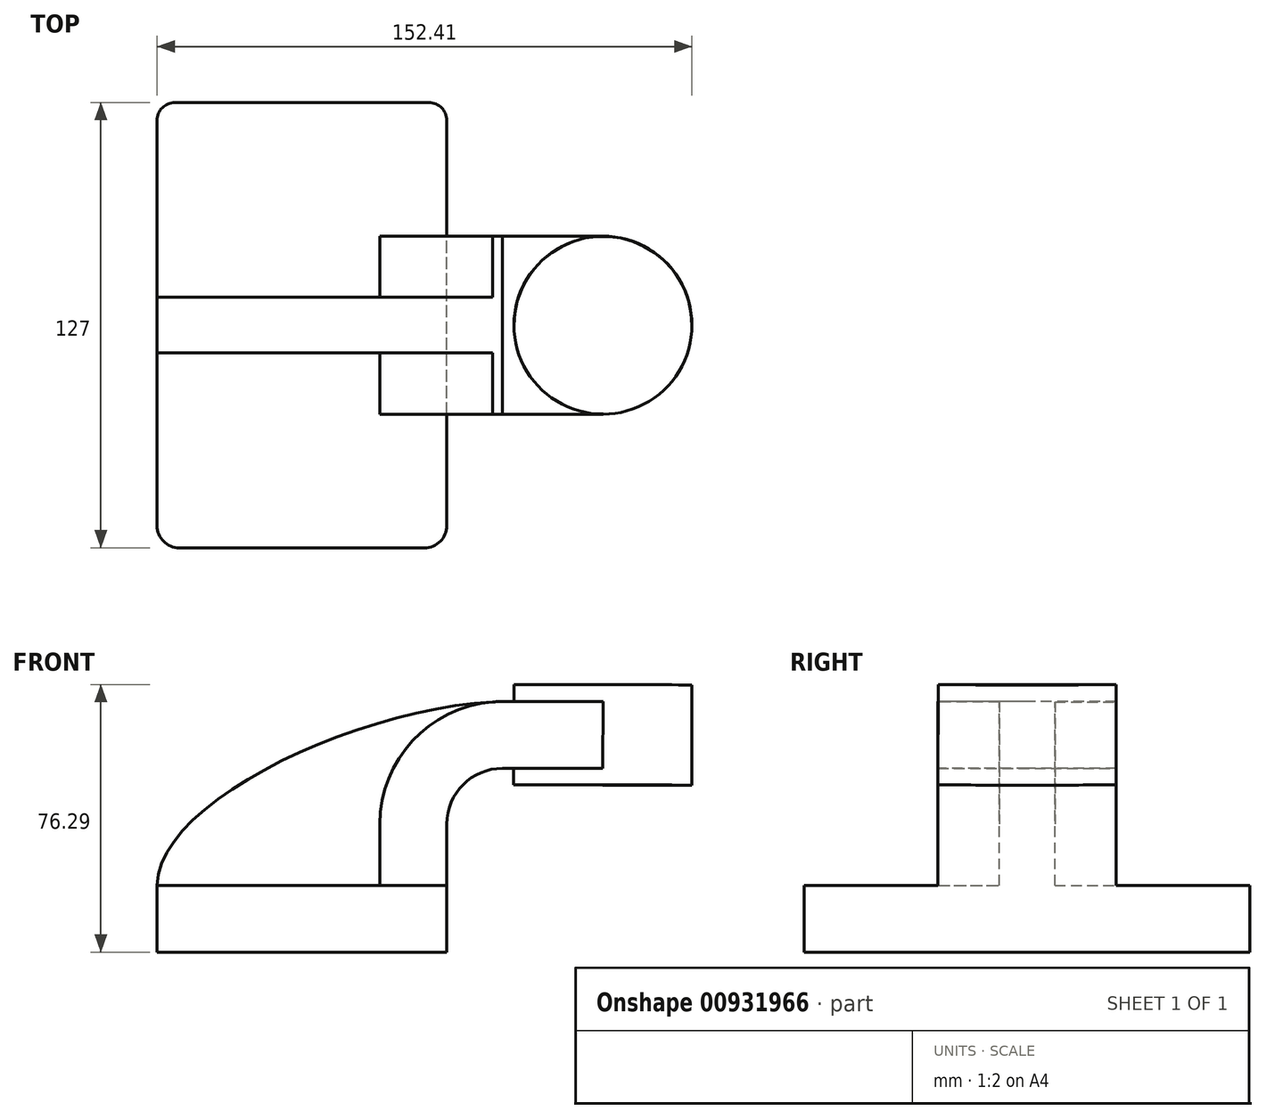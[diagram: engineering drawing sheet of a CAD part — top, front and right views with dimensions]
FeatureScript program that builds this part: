
annotation { "Feature Type Name" : "Feature", "Feature Type Description" : "" }
export const myFeature = defineFeature(function(context is Context, id is Id, definition is map)
    precondition{}
    {
        {
            var Q0;
            Q0=qCreatedBy(makeId("Front.planeOp"),FACE);
            var sketch = newSketch(context, id + "F0", { "sketchPlane" : qUnion([Q0])});
            skLineSegment(sketch, "E0.bottom", {"start": v(41.28, -9.52) * mm, "end": v(-41.28, -9.53) * mm});
            skLineSegment(sketch, "E0.top", {"start": v(41.27, 9.53) * mm, "end": v(-41.28, 9.53) * mm});
            skLineSegment(sketch, "E0.left", {"start": v(41.28, -9.52) * mm, "end": v(41.28, 9.53) * mm});
            skLineSegment(sketch, "E0.right", {"start": v(-41.28, -9.53) * mm, "end": v(-41.28, 9.53) * mm});
            skPoint(sketch, "E0.middle", {"position": v(0, 0) * mm});
            skLineSegment(sketch, "E1.bottom", {"start": v(60.32, 66.68) * mm, "end": v(111.12, 66.68) * mm});
            skLineSegment(sketch, "E1.top", {"start": v(60.32, 38.1) * mm, "end": v(111.12, 38.1) * mm});
            skLineSegment(sketch, "E1.left", {"start": v(60.32, 66.68) * mm, "end": v(60.32, 38.1) * mm});
            skLineSegment(sketch, "E1.right", {"start": v(111.13, 66.68) * mm, "end": v(111.13, 38.1) * mm});
            skPoint(sketch, "E1.middle", {"position": v(85.72, 52.39) * mm});
            skLineSegment(sketch, "E2", {"start": v(41.27, 9.53) * mm, "end": v(41.27, 27) * mm});
            skArc(sketch, "E3", {"start": v(41.27, 27) * mm, "mid": v(45.92, 38.23) * mm, "end": v(57.15, 42.88) * mm});
            skLineSegment(sketch, "E4", {"start": v(57.15, 42.88) * mm, "end": v(85.77, 42.88) * mm});
            skLineSegment(sketch, "E5.0", {"start": v(57.15, 61.93) * mm, "end": v(85.77, 61.93) * mm});
            skArc(sketch, "E5.1", {"start": v(22.23, 27) * mm, "mid": v(32.45, 51.7) * mm, "end": v(57.15, 61.93) * mm});
            skLineSegment(sketch, "E5.2", {"start": v(22.22, 9.53) * mm, "end": v(22.22, 27) * mm});
            skLineSegment(sketch, "E6", {"start": v(85.72, 38.1) * mm, "end": v(85.77, 66.68) * mm});
            skFitSpline(sketch, "E7", {"points": [v(-41.28, 9.52) * mm, v(57.15, 61.93) * mm], "startDerivative": vector(0.34, 72.37) * mm, "endDerivative": vector(119.63, 3.02) * mm});
            skSolve(sketch);
        }
        {
            var Q0;
            Q0=makeQuery(id+"F0.imprint","IMPRINT",FACE,{"disambiguationData":[TD([[makeQuery(id+"F0.imprint","IMPRINT",EDGE,{"derivedFrom":sQuery(id+"F0.wireOp",EDGE,"E0.bottom")}),-1.0]])]});
            extrude(context, id + "F1", {"entities" : qUnion([Q0]), "endBound" : BoundingType.SYMMETRIC, "depth" : 127 * mm, "offsetDistance" : 25.4 * mm});
        }
        {
            var Q0;
            {var subQ3=sQuery(id+"F0.wireOp",EDGE,"E5.2");Q0=makeQuery(id+"F0.imprint","IMPRINT",FACE,{"disambiguationData":[TD([[makeQuery(id+"F0.imprint","IMPRINT",EDGE,{"derivedFrom":subQ3}),1.0]])]});}
            extrude(context, id + "F2", {"entities" : qUnion([Q0]), "operationType" : NewBodyOperationType.ADD, "endBound" : BoundingType.SYMMETRIC, "depth" : 15.88 * mm, "offsetDistance" : 25.4 * mm});
        }
        {
            var Q0;
            {var subQ1=sQuery(id+"F0.wireOp",EDGE,"E2");Q0=makeQuery(id+"F0.imprint","IMPRINT",FACE,{"disambiguationData":[TD([[makeQuery(id+"F0.imprint","IMPRINT",EDGE,{"derivedFrom":subQ1}),1.0]])]});}
            var Q1;
            {var subQ0=sQuery(id+"F0.wireOp",EDGE,"E5.0");var subQ1=sQuery(id+"F0.wireOp",EDGE,"E1.left");var subQ2=makeQuery(id+"F0.imprint","INTERSECT",VERTEX,{"derivedFrom":[subQ1,subQ0]});Q1=makeQuery(id+"F0.imprint","IMPRINT",FACE,{"disambiguationData":[TD([[makeQuery(id+"F0.imprint","IMPRINT",EDGE,{"disambiguationData":[TD([[subQ2,-1.0]])],"derivedFrom":subQ1}),1.0]])]});}
            extrude(context, id + "F3", {"entities" : qUnion([Q0, Q1]), "operationType" : NewBodyOperationType.ADD, "endBound" : BoundingType.SYMMETRIC, "depth" : 50.8 * mm, "offsetDistance" : 25.4 * mm});
        }
        {
            var Q0;
            {var subQ4=sQuery(id+"F0.wireOp",EDGE,"E1.right");Q0=makeQuery(id+"F0.imprint","IMPRINT",FACE,{"disambiguationData":[TD([[makeQuery(id+"F0.imprint","IMPRINT",EDGE,{"derivedFrom":subQ4}),-1.0]])]});}
            var Q1;
            Q1=sQuery(id+"F0.wireOp",EDGE,"E6");
            revolve(context, id + "F4", {"operationType" : NewBodyOperationType.ADD, "surfaceOperationType" : NewSurfaceOperationType.NEW, "entities" : qUnion([Q0]), "axis" : qUnion([Q1]), "revolveType" : RevolveType.FULL});
        }
        {
            var Q0;
            Q0=makeQuery(id+"F1.opExtrude","CAP_EDGE",EDGE,{"disambiguationData":[OSD([sQuery(id+"F0.wireOp",EDGE,"E0.left")])],"isStart":false});
            var Q1;
            Q1=makeQuery(id+"F1.opExtrude","CAP_EDGE",EDGE,{"disambiguationData":[OSD([sQuery(id+"F0.wireOp",EDGE,"E0.right")])],"isStart":false});
            fillet(context, id + "F5", {"entities" : qUnion([Q0, Q1]), "radius" : 6.35 * mm, "tangentPropagation" : true, "allowEdgeOverflow" : false});
        }
        {
            var Q0;
            Q0=makeQuery(id+"F1.opExtrude","CAP_EDGE",EDGE,{"disambiguationData":[OSD([sQuery(id+"F0.wireOp",EDGE,"E0.right")])],"isStart":true});
            var Q1;
            Q1=makeQuery(id+"F1.opExtrude","CAP_EDGE",EDGE,{"disambiguationData":[OSD([sQuery(id+"F0.wireOp",EDGE,"E0.left")])],"isStart":true});
            fillet(context, id + "F6", {"entities" : qUnion([Q0, Q1]), "radius" : 5.08 * mm, "tangentPropagation" : true, "allowEdgeOverflow" : false});
        }
    });
